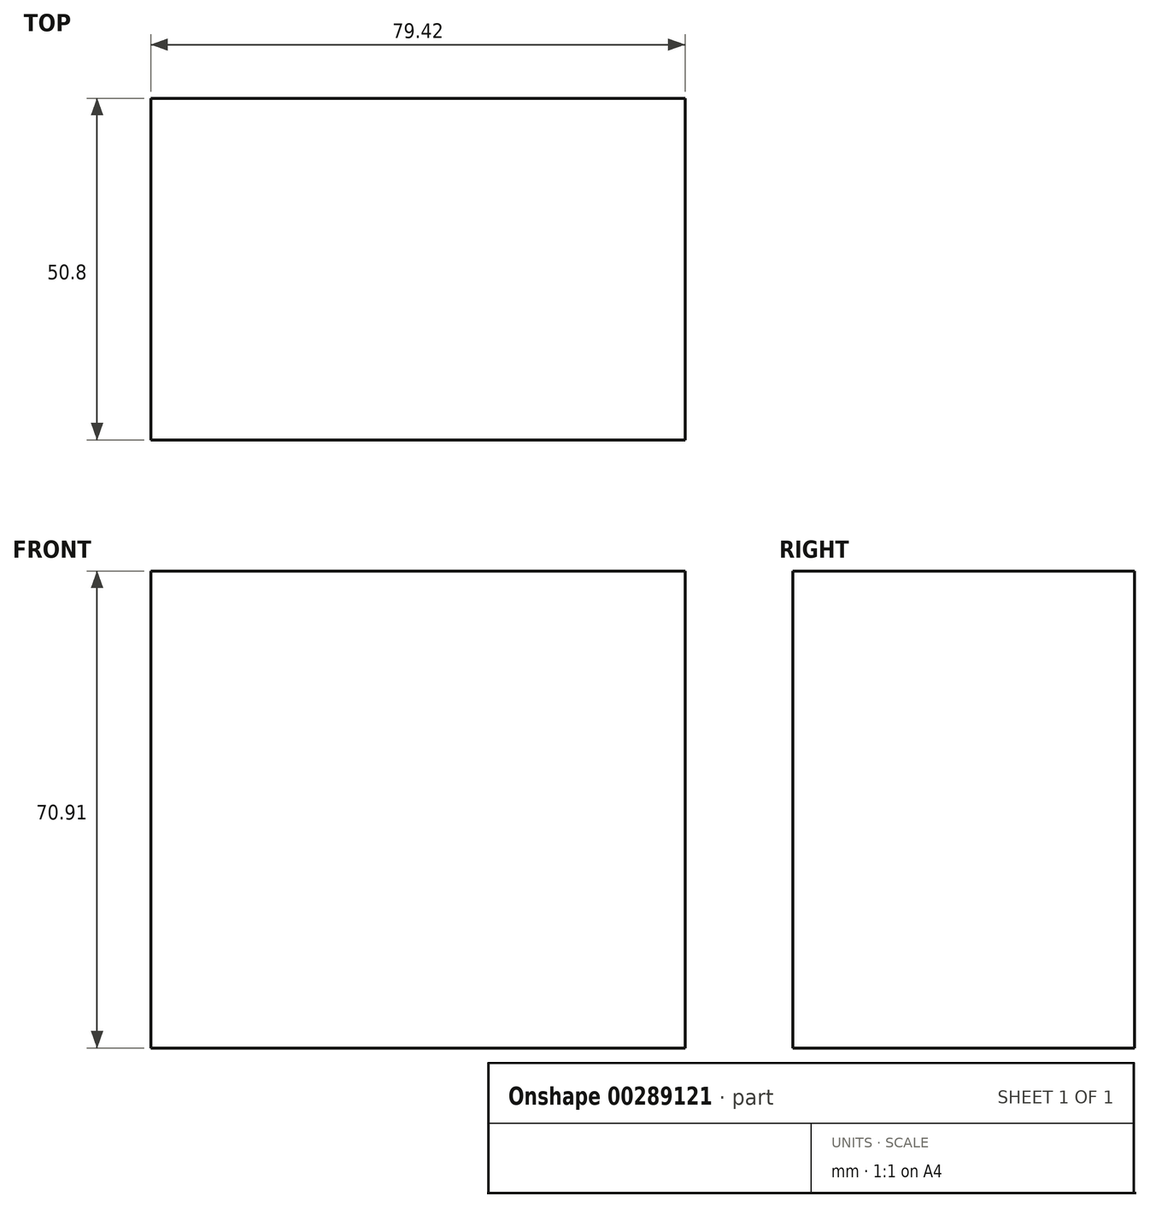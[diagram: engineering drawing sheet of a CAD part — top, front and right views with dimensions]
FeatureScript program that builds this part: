
annotation { "Feature Type Name" : "Feature", "Feature Type Description" : "" }
export const myFeature = defineFeature(function(context is Context, id is Id, definition is map)
    precondition{}
    {
        {
            var Q0;
            Q0=qCreatedBy(makeId("Front.planeOp"),FACE);
            var sketch = newSketch(context, id + "F0", { "sketchPlane" : qUnion([Q0])});
            skLineSegment(sketch, "E0.bottom", {"start": v(-47.27, 45.5) * mm, "end": v(32.15, 45.5) * mm});
            skLineSegment(sketch, "E0.top", {"start": v(-47.27, -25.4) * mm, "end": v(32.15, -25.4) * mm});
            skLineSegment(sketch, "E0.left", {"start": v(-47.27, 45.5) * mm, "end": v(-47.27, -25.4) * mm});
            skLineSegment(sketch, "E0.right", {"start": v(32.15, 45.5) * mm, "end": v(32.15, -25.4) * mm});
            skSolve(sketch);
        }
        {
            var Q0;
            Q0 = qSketchRegion(id + "F0", true);
            extrude(context, id + "F1", {"entities" : qUnion([Q0]), "depth" : 50.8 * mm});
        }
    });
